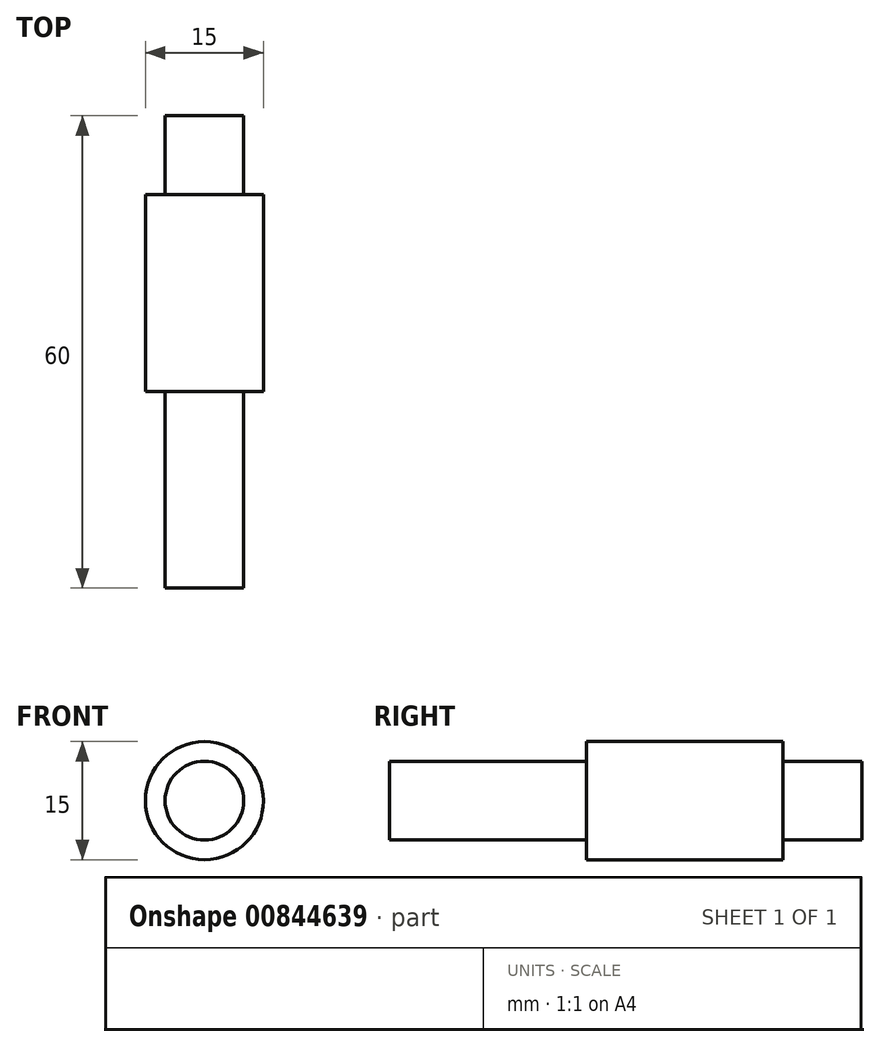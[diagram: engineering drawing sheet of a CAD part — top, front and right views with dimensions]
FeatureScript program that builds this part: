
annotation { "Feature Type Name" : "Feature", "Feature Type Description" : "" }
export const myFeature = defineFeature(function(context is Context, id is Id, definition is map)
    precondition{}
    {
        {
            var Q0;
            Q0=qCreatedBy(makeId("Front.planeOp"),FACE);
            var sketch = newSketch(context, id + "F0", { "sketchPlane" : qUnion([Q0])});
            skCircle(sketch, "E0", {"center": v(0, 0) * mm, "radius": 5 * mm});
            skSolve(sketch);
        }
        {
            var Q0;
            Q0=makeQuery(id+"F0.imprint","IMPRINT",FACE,{"disambiguationData":[TD([[makeQuery(id+"F0.imprint","IMPRINT",EDGE,{"derivedFrom":sQuery(id+"F0.wireOp",EDGE,"E0")}),1.0]])]});
            extrude(context, id + "F1", {"entities" : qUnion([Q0]), "depth" : 10 * mm, "offsetDistance" : 25 * mm});
        }
        {
            var Q0;
            Q0=makeQuery(id+"F1.opExtrude","CAP_FACE",FACE,{"disambiguationData":[OSD([sQuery(id+"F0.wireOp",EDGE,"E0")])],"isStart":false});
            var sketch = newSketch(context, id + "F2", { "sketchPlane" : qUnion([Q0])});
            skCircle(sketch, "E1", {"center": v(0, 0) * mm, "radius": 7.5 * mm});
            skSolve(sketch);
        }
        {
            var Q0;
            Q0 = qSketchRegion(id + "F2", true);
            extrude(context, id + "F3", {"entities" : qUnion([Q0]), "operationType" : NewBodyOperationType.ADD, "depth" : 25 * mm, "offsetDistance" : 25 * mm});
        }
        {
            var Q0;
            Q0=makeQuery(id+"F3.opExtrude","CAP_FACE",FACE,{"disambiguationData":[OSD([sQuery(id+"F2.wireOp",EDGE,"E1")])],"isStart":false});
            var sketch = newSketch(context, id + "F4", { "sketchPlane" : qUnion([Q0])});
            skCircle(sketch, "E2", {"center": v(0, 0) * mm, "radius": 5 * mm});
            skSolve(sketch);
        }
        {
            var Q0;
            Q0=makeQuery(id+"F4.imprint","IMPRINT",FACE,{"disambiguationData":[TD([[makeQuery(id+"F4.imprint","IMPRINT",EDGE,{"derivedFrom":sQuery(id+"F4.wireOp",EDGE,"E2")}),1.0]])]});
            extrude(context, id + "F5", {"entities" : qUnion([Q0]), "operationType" : NewBodyOperationType.ADD, "depth" : 25 * mm, "offsetDistance" : 25 * mm});
        }
    });
